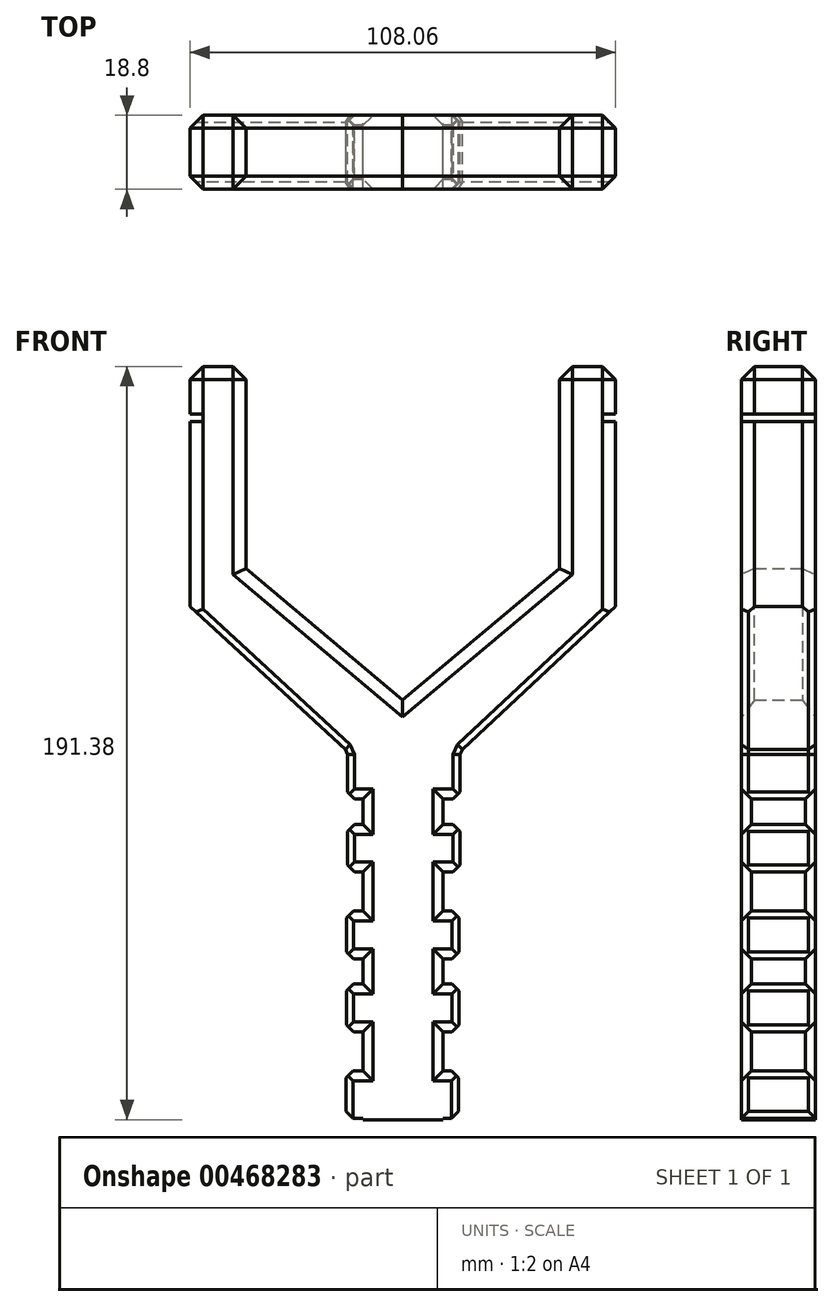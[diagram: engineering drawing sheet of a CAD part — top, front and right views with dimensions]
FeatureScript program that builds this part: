
annotation { "Feature Type Name" : "Feature", "Feature Type Description" : "" }
export const myFeature = defineFeature(function(context is Context, id is Id, definition is map)
    precondition{}
    {
        {
            var Q0;
            Q0=qCreatedBy(makeId("Front.planeOp"),FACE);
            var sketch = newSketch(context, id + "F0", { "sketchPlane" : qUnion([Q0])});
            skLineSegment(sketch, "E0.bottom", {"start": v(-10.06, -21.6) * mm, "end": v(10.26, -21.6) * mm});
            skLineSegment(sketch, "E0.top", {"start": v(-10.06, -123.2) * mm, "end": v(10.26, -123.2) * mm});
            skLineSegment(sketch, "E0.left", {"start": v(-10.06, -21.6) * mm, "end": v(-10.06, -123.2) * mm});
            skLineSegment(sketch, "E0.right", {"start": v(10.26, -21.6) * mm, "end": v(10.26, -123.2) * mm});
            skLineSegment(sketch, "E1.bottom", {"start": v(-14, -29.67) * mm, "end": v(14.56, -29.67) * mm});
            skLineSegment(sketch, "E1.top", {"start": v(-14, -41.76) * mm, "end": v(14.56, -41.76) * mm});
            skLineSegment(sketch, "E1.left", {"start": v(-14, -29.67) * mm, "end": v(-14, -41.76) * mm});
            skLineSegment(sketch, "E1.right", {"start": v(14.56, -29.67) * mm, "end": v(14.56, -41.76) * mm});
            skLineSegment(sketch, "E2.0.1.0", {"start": v(-14, -48.22) * mm, "end": v(14.56, -48.22) * mm});
            skLineSegment(sketch, "E2.0.1.1", {"start": v(-14, -60.3) * mm, "end": v(14.56, -60.3) * mm});
            skLineSegment(sketch, "E2.0.1.2", {"start": v(14.56, -48.22) * mm, "end": v(14.56, -60.3) * mm});
            skLineSegment(sketch, "E2.0.1.3", {"start": v(-14, -48.22) * mm, "end": v(-14, -60.3) * mm});
            skLineSegment(sketch, "E2.1.0.0", {"start": v(-14.22, -70.2) * mm, "end": v(14.34, -70.2) * mm});
            skLineSegment(sketch, "E2.1.0.1", {"start": v(-14.22, -82.3) * mm, "end": v(14.34, -82.3) * mm});
            skLineSegment(sketch, "E2.1.0.2", {"start": v(14.34, -70.2) * mm, "end": v(14.34, -82.3) * mm});
            skLineSegment(sketch, "E2.1.0.3", {"start": v(-14.22, -70.2) * mm, "end": v(-14.22, -82.3) * mm});
            skLineSegment(sketch, "E2.1.1.0", {"start": v(-14.22, -88.75) * mm, "end": v(14.34, -88.75) * mm});
            skLineSegment(sketch, "E2.1.1.1", {"start": v(-14.22, -100.84) * mm, "end": v(14.34, -100.84) * mm});
            skLineSegment(sketch, "E2.1.1.2", {"start": v(14.34, -88.75) * mm, "end": v(14.34, -100.84) * mm});
            skLineSegment(sketch, "E2.1.1.3", {"start": v(-14.22, -88.75) * mm, "end": v(-14.22, -100.84) * mm});
            skLineSegment(sketch, "E2.2.0.0", {"start": v(-14.44, -110.74) * mm, "end": v(14.13, -110.74) * mm});
            skLineSegment(sketch, "E2.2.0.1", {"start": v(-14.44, -122.83) * mm, "end": v(14.13, -122.83) * mm});
            skLineSegment(sketch, "E2.2.0.2", {"start": v(14.13, -110.74) * mm, "end": v(14.13, -122.83) * mm});
            skLineSegment(sketch, "E2.2.0.3", {"start": v(-14.44, -110.74) * mm, "end": v(-14.44, -122.83) * mm});
            skLineSegment(sketch, "E2.direction1", {"start": v(-14, -41.76) * mm, "end": v(-14.22, -82.3) * mm, "construction": true});
            skLineSegment(sketch, "E2.direction2", {"start": v(-14, -41.76) * mm, "end": v(-14, -60.3) * mm, "construction": true});
            skLineSegment(sketch, "E3.bottom", {"start": v(-54.03, 7.22) * mm, "end": v(-43.42, 19.87) * mm});
            skLineSegment(sketch, "E3.top", {"start": v(-10.06, -29.67) * mm, "end": v(0.55, -17.03) * mm});
            skLineSegment(sketch, "E3.left", {"start": v(-54.03, 7.22) * mm, "end": v(-10.06, -29.67) * mm});
            skLineSegment(sketch, "E3.right", {"start": v(-43.42, 19.87) * mm, "end": v(0.55, -17.03) * mm});
            skLineSegment(sketch, "E4.MirrorCS", {"start": v(43.42, 19.87) * mm, "end": v(-0.55, -17.03) * mm});
            skLineSegment(sketch, "E5.MirrorCS", {"start": v(54.03, 7.22) * mm, "end": v(43.42, 19.87) * mm});
            skLineSegment(sketch, "E6.MirrorCS", {"start": v(54.03, 7.22) * mm, "end": v(10.06, -29.67) * mm});
            skLineSegment(sketch, "E7.MirrorCS", {"start": v(10.06, -29.67) * mm, "end": v(-0.55, -17.03) * mm});
            skLineSegment(sketch, "E8.bottom", {"start": v(-54.03, 68.18) * mm, "end": v(-39.8, 68.18) * mm});
            skLineSegment(sketch, "E8.top", {"start": v(-54.03, 7.22) * mm, "end": v(-39.8, 7.22) * mm});
            skLineSegment(sketch, "E8.left", {"start": v(-54.03, 68.18) * mm, "end": v(-54.03, 7.22) * mm});
            skLineSegment(sketch, "E8.right", {"start": v(-39.8, 68.18) * mm, "end": v(-39.8, 7.22) * mm});
            skLineSegment(sketch, "E9.bottom", {"start": v(39.8, 68.18) * mm, "end": v(54.03, 68.18) * mm});
            skLineSegment(sketch, "E9.top", {"start": v(39.8, 7.22) * mm, "end": v(54.03, 7.22) * mm});
            skLineSegment(sketch, "E9.left", {"start": v(39.8, 68.18) * mm, "end": v(39.8, 7.22) * mm});
            skLineSegment(sketch, "E9.right", {"start": v(54.03, 68.18) * mm, "end": v(54.03, 7.22) * mm});
            skFitSpline(sketch, "E10", {"points": [v(-54.03, 7.22) * mm, v(-14, -29.67) * mm], "startDerivative": vector(40.02, -36.9) * mm, "endDerivative": vector(40.02, -36.9) * mm});
            skFitSpline(sketch, "E11", {"points": [v(14.56, -29.67) * mm, v(54.03, 7.22) * mm], "startDerivative": vector(39.47, 36.9) * mm, "endDerivative": vector(39.47, 36.9) * mm});
            skLineSegment(sketch, "E12.bottom", {"start": v(-54.03, 56.1) * mm, "end": v(-50.76, 56.1) * mm});
            skLineSegment(sketch, "E12.top", {"start": v(-54.03, 54.23) * mm, "end": v(-50.76, 54.23) * mm});
            skLineSegment(sketch, "E12.left", {"start": v(-54.03, 56.1) * mm, "end": v(-54.03, 54.23) * mm});
            skLineSegment(sketch, "E12.right", {"start": v(-50.76, 56.1) * mm, "end": v(-50.76, 54.23) * mm});
            skLineSegment(sketch, "E13.MirrorCS", {"start": v(54.03, 56.1) * mm, "end": v(50.76, 56.1) * mm});
            skLineSegment(sketch, "E14.MirrorCS", {"start": v(54.03, 54.23) * mm, "end": v(50.76, 54.23) * mm});
            skLineSegment(sketch, "E15.MirrorCS", {"start": v(50.76, 56.1) * mm, "end": v(50.76, 54.23) * mm});
            skLineSegment(sketch, "E16.MirrorCS", {"start": v(54.03, 56.1) * mm, "end": v(54.03, 54.23) * mm});
            skSolve(sketch);
        }
        {
            var Q0;
            {var subQ0=sQuery(id+"F0.wireOp",EDGE,"E3.top");var subQ1=sQuery(id+"F0.wireOp",EDGE,"E0.bottom");var subQ2=makeQuery(id+"F0.imprint","INTERSECT",VERTEX,{"derivedFrom":[subQ1,subQ0]});Q0=makeQuery(id+"F0.imprint","IMPRINT",FACE,{"disambiguationData":[TD([[makeQuery(id+"F0.imprint","IMPRINT",EDGE,{"disambiguationData":[TD([[subQ2,-1.0]])],"derivedFrom":subQ1}),-1.0]])]});}
            var Q1;
            {var subQ0=sQuery(id+"F0.wireOp",EDGE,"E3.top");var subQ1=sQuery(id+"F0.wireOp",EDGE,"E0.bottom");var subQ2=makeQuery(id+"F0.imprint","INTERSECT",VERTEX,{"derivedFrom":[subQ1,subQ0]});Q1=makeQuery(id+"F0.imprint","IMPRINT",FACE,{"disambiguationData":[TD([[makeQuery(id+"F0.imprint","IMPRINT",EDGE,{"disambiguationData":[TD([[subQ2,-1.0]])],"derivedFrom":subQ1}),1.0]])]});}
            var Q2;
            {var subQ0=sQuery(id+"F0.wireOp",EDGE,"E2.1.0.1");var subQ1=sQuery(id+"F0.wireOp",EDGE,"E0.left");var subQ2=makeQuery(id+"F0.imprint","INTERSECT",VERTEX,{"derivedFrom":[subQ1,subQ0]});Q2=makeQuery(id+"F0.imprint","IMPRINT",FACE,{"disambiguationData":[TD([[makeQuery(id+"F0.imprint","IMPRINT",EDGE,{"disambiguationData":[TD([[subQ2,-1.0]])],"derivedFrom":subQ1}),1.0]])]});}
            var Q3;
            {var subQ0=sQuery(id+"F0.wireOp",EDGE,"E3.bottom");Q3=makeQuery(id+"F0.imprint","IMPRINT",FACE,{"disambiguationData":[TD([[makeQuery(id+"F0.imprint","IMPRINT",EDGE,{"derivedFrom":subQ0}),-1.0]])]});}
            var Q4;
            {var subQ0=sQuery(id+"F0.wireOp",EDGE,"E2.1.1.0");var subQ1=sQuery(id+"F0.wireOp",EDGE,"E0.left");var subQ2=makeQuery(id+"F0.imprint","INTERSECT",VERTEX,{"derivedFrom":[subQ1,subQ0]});Q4=makeQuery(id+"F0.imprint","IMPRINT",FACE,{"disambiguationData":[TD([[makeQuery(id+"F0.imprint","IMPRINT",EDGE,{"disambiguationData":[TD([[subQ2,-1.0]])],"derivedFrom":subQ1}),1.0]])]});}
            var Q5;
            {var subQ0=sQuery(id+"F0.wireOp",EDGE,"E1.top");var subQ1=sQuery(id+"F0.wireOp",EDGE,"E0.left");var subQ2=makeQuery(id+"F0.imprint","INTERSECT",VERTEX,{"derivedFrom":[subQ1,subQ0]});Q5=makeQuery(id+"F0.imprint","IMPRINT",FACE,{"disambiguationData":[TD([[makeQuery(id+"F0.imprint","IMPRINT",EDGE,{"disambiguationData":[TD([[subQ2,-1.0]])],"derivedFrom":subQ1}),1.0]])]});}
            var Q6;
            {var subQ0=sQuery(id+"F0.wireOp",EDGE,"E2.1.1.1");var subQ1=sQuery(id+"F0.wireOp",EDGE,"E0.left");var subQ2=makeQuery(id+"F0.imprint","INTERSECT",VERTEX,{"derivedFrom":[subQ1,subQ0]});Q6=makeQuery(id+"F0.imprint","IMPRINT",FACE,{"disambiguationData":[TD([[makeQuery(id+"F0.imprint","IMPRINT",EDGE,{"disambiguationData":[TD([[subQ2,-1.0]])],"derivedFrom":subQ1}),1.0]])]});}
            var Q7;
            {var subQ0=sQuery(id+"F0.wireOp",EDGE,"E2.0.1.1");var subQ1=sQuery(id+"F0.wireOp",EDGE,"E0.left");var subQ2=makeQuery(id+"F0.imprint","INTERSECT",VERTEX,{"derivedFrom":[subQ1,subQ0]});Q7=makeQuery(id+"F0.imprint","IMPRINT",FACE,{"disambiguationData":[TD([[makeQuery(id+"F0.imprint","IMPRINT",EDGE,{"disambiguationData":[TD([[subQ2,-1.0]])],"derivedFrom":subQ1}),1.0]])]});}
            var Q8;
            {var subQ6=sQuery(id+"F0.wireOp",EDGE,"E9.top");Q8=makeQuery(id+"F0.imprint","IMPRINT",FACE,{"disambiguationData":[TD([[makeQuery(id+"F0.imprint","IMPRINT",EDGE,{"derivedFrom":subQ6}),-1.0]])]});}
            var Q9;
            {var subQ5=sQuery(id+"F0.wireOp",EDGE,"E2.0.1.3");Q9=makeQuery(id+"F0.imprint","IMPRINT",FACE,{"disambiguationData":[TD([[makeQuery(id+"F0.imprint","IMPRINT",EDGE,{"derivedFrom":subQ5}),1.0]])]});}
            var Q10;
            {var subQ5=sQuery(id+"F0.wireOp",EDGE,"E2.1.0.3");Q10=makeQuery(id+"F0.imprint","IMPRINT",FACE,{"disambiguationData":[TD([[makeQuery(id+"F0.imprint","IMPRINT",EDGE,{"derivedFrom":subQ5}),1.0]])]});}
            var Q11;
            {var subQ5=sQuery(id+"F0.wireOp",EDGE,"E2.1.1.3");Q11=makeQuery(id+"F0.imprint","IMPRINT",FACE,{"disambiguationData":[TD([[makeQuery(id+"F0.imprint","IMPRINT",EDGE,{"derivedFrom":subQ5}),1.0]])]});}
            var Q12;
            {var subQ5=sQuery(id+"F0.wireOp",EDGE,"E2.2.0.3");Q12=makeQuery(id+"F0.imprint","IMPRINT",FACE,{"disambiguationData":[TD([[makeQuery(id+"F0.imprint","IMPRINT",EDGE,{"derivedFrom":subQ5}),1.0]])]});}
            var Q13;
            {var subQ5=sQuery(id+"F0.wireOp",EDGE,"E2.0.1.2");Q13=makeQuery(id+"F0.imprint","IMPRINT",FACE,{"disambiguationData":[TD([[makeQuery(id+"F0.imprint","IMPRINT",EDGE,{"derivedFrom":subQ5}),-1.0]])]});}
            var Q14;
            {var subQ5=sQuery(id+"F0.wireOp",EDGE,"E2.2.0.2");Q14=makeQuery(id+"F0.imprint","IMPRINT",FACE,{"disambiguationData":[TD([[makeQuery(id+"F0.imprint","IMPRINT",EDGE,{"derivedFrom":subQ5}),-1.0]])]});}
            var Q15;
            {var subQ5=sQuery(id+"F0.wireOp",EDGE,"E2.1.0.2");Q15=makeQuery(id+"F0.imprint","IMPRINT",FACE,{"disambiguationData":[TD([[makeQuery(id+"F0.imprint","IMPRINT",EDGE,{"derivedFrom":subQ5}),-1.0]])]});}
            var Q16;
            {var subQ5=sQuery(id+"F0.wireOp",EDGE,"E2.1.1.2");Q16=makeQuery(id+"F0.imprint","IMPRINT",FACE,{"disambiguationData":[TD([[makeQuery(id+"F0.imprint","IMPRINT",EDGE,{"derivedFrom":subQ5}),-1.0]])]});}
            var Q17;
            {var subQ2=sQuery(id+"F0.wireOp",EDGE,"E3.bottom");Q17=makeQuery(id+"F0.imprint","IMPRINT",FACE,{"disambiguationData":[TD([[makeQuery(id+"F0.imprint","IMPRINT",EDGE,{"derivedFrom":subQ2}),1.0]])]});}
            var Q18;
            {var subQ4=sQuery(id+"F0.wireOp",EDGE,"E5.MirrorCS");Q18=makeQuery(id+"F0.imprint","IMPRINT",FACE,{"disambiguationData":[TD([[makeQuery(id+"F0.imprint","IMPRINT",EDGE,{"derivedFrom":subQ4}),-1.0]])]});}
            var Q19;
            {var subQ0=sQuery(id+"F0.wireOp",EDGE,"E0.left");var subQ1=sQuery(id+"F0.wireOp",EDGE,"E0.bottom");var subQ2=makeQuery(id+"F0.imprint","INTERSECT",VERTEX,{"derivedFrom":[subQ1,subQ0]});Q19=makeQuery(id+"F0.imprint","IMPRINT",FACE,{"disambiguationData":[TD([[makeQuery(id+"F0.imprint","IMPRINT",EDGE,{"disambiguationData":[TD([[subQ2,-1.0]])],"derivedFrom":subQ1}),-1.0]])]});}
            var Q20;
            {var subQ5=sQuery(id+"F0.wireOp",EDGE,"E1.left");Q20=makeQuery(id+"F0.imprint","IMPRINT",FACE,{"disambiguationData":[TD([[makeQuery(id+"F0.imprint","IMPRINT",EDGE,{"derivedFrom":subQ5}),1.0]])]});}
            var Q21;
            {var subQ0=sQuery(id+"F0.wireOp",EDGE,"E2.0.1.0");var subQ1=sQuery(id+"F0.wireOp",EDGE,"E0.left");var subQ2=makeQuery(id+"F0.imprint","INTERSECT",VERTEX,{"derivedFrom":[subQ1,subQ0]});Q21=makeQuery(id+"F0.imprint","IMPRINT",FACE,{"disambiguationData":[TD([[makeQuery(id+"F0.imprint","IMPRINT",EDGE,{"disambiguationData":[TD([[subQ2,-1.0]])],"derivedFrom":subQ1}),1.0]])]});}
            var Q22;
            {var subQ0=sQuery(id+"F0.wireOp",EDGE,"E0.right");var subQ1=sQuery(id+"F0.wireOp",EDGE,"E0.bottom");var subQ2=makeQuery(id+"F0.imprint","INTERSECT",VERTEX,{"derivedFrom":[subQ1,subQ0]});Q22=makeQuery(id+"F0.imprint","IMPRINT",FACE,{"disambiguationData":[TD([[makeQuery(id+"F0.imprint","IMPRINT",EDGE,{"disambiguationData":[TD([[subQ2,1.0]])],"derivedFrom":subQ1}),-1.0]])]});}
            var Q23;
            {var subQ0=sQuery(id+"F0.wireOp",EDGE,"E5.MirrorCS");Q23=makeQuery(id+"F0.imprint","IMPRINT",FACE,{"disambiguationData":[TD([[makeQuery(id+"F0.imprint","IMPRINT",EDGE,{"derivedFrom":subQ0}),1.0]])]});}
            var Q24;
            {var subQ0=sQuery(id+"F0.wireOp",EDGE,"E2.2.0.0");var subQ1=sQuery(id+"F0.wireOp",EDGE,"E0.left");var subQ2=makeQuery(id+"F0.imprint","INTERSECT",VERTEX,{"derivedFrom":[subQ1,subQ0]});Q24=makeQuery(id+"F0.imprint","IMPRINT",FACE,{"disambiguationData":[TD([[makeQuery(id+"F0.imprint","IMPRINT",EDGE,{"disambiguationData":[TD([[subQ2,-1.0]])],"derivedFrom":subQ1}),1.0]])]});}
            var Q25;
            {var subQ5=sQuery(id+"F0.wireOp",EDGE,"E1.right");Q25=makeQuery(id+"F0.imprint","IMPRINT",FACE,{"disambiguationData":[TD([[makeQuery(id+"F0.imprint","IMPRINT",EDGE,{"derivedFrom":subQ5}),-1.0]])]});}
            var Q26;
            {var subQ2=sQuery(id+"F0.wireOp",EDGE,"E0.right");var subQ6=sQuery(id+"F0.wireOp",EDGE,"E1.top");var subQ7=makeQuery(id+"F0.imprint","INTERSECT",VERTEX,{"derivedFrom":[subQ2,subQ6]});Q26=makeQuery(id+"F0.imprint","IMPRINT",FACE,{"disambiguationData":[TD([[makeQuery(id+"F0.imprint","IMPRINT",EDGE,{"disambiguationData":[TD([[subQ7,1.0]])],"derivedFrom":subQ2}),-1.0]])]});}
            var Q27;
            {var subQ0=sQuery(id+"F0.wireOp",EDGE,"E2.1.0.0");var subQ1=sQuery(id+"F0.wireOp",EDGE,"E0.left");var subQ2=makeQuery(id+"F0.imprint","INTERSECT",VERTEX,{"derivedFrom":[subQ1,subQ0]});Q27=makeQuery(id+"F0.imprint","IMPRINT",FACE,{"disambiguationData":[TD([[makeQuery(id+"F0.imprint","IMPRINT",EDGE,{"disambiguationData":[TD([[subQ2,-1.0]])],"derivedFrom":subQ1}),1.0]])]});}
            var Q28;
            {var subQ2=sQuery(id+"F0.wireOp",EDGE,"E3.left");Q28=makeQuery(id+"F0.imprint","IMPRINT",FACE,{"disambiguationData":[TD([[makeQuery(id+"F0.imprint","IMPRINT",EDGE,{"derivedFrom":subQ2}),-1.0]])]});}
            var Q29;
            {var subQ0=sQuery(id+"F0.wireOp",EDGE,"E3.left");Q29=makeQuery(id+"F0.imprint","IMPRINT",FACE,{"disambiguationData":[TD([[makeQuery(id+"F0.imprint","IMPRINT",EDGE,{"derivedFrom":subQ0}),1.0]])]});}
            var Q30;
            {var subQ5=sQuery(id+"F0.wireOp",EDGE,"E11");Q30=makeQuery(id+"F0.imprint","IMPRINT",FACE,{"disambiguationData":[TD([[makeQuery(id+"F0.imprint","IMPRINT",EDGE,{"derivedFrom":subQ5}),1.0]])]});}
            var Q31;
            {var subQ0=sQuery(id+"F0.wireOp",EDGE,"E0.top");Q31=makeQuery(id+"F0.imprint","IMPRINT",FACE,{"disambiguationData":[TD([[makeQuery(id+"F0.imprint","IMPRINT",EDGE,{"derivedFrom":subQ0}),1.0]])]});}
            var Q32;
            {var subQ0=sQuery(id+"F0.wireOp",EDGE,"E3.right");var subQ1=sQuery(id+"F0.wireOp",EDGE,"E3.top");var subQ2=makeQuery(id+"F0.imprint","INTERSECT",VERTEX,{"derivedFrom":[subQ1,subQ0]});Q32=makeQuery(id+"F0.imprint","IMPRINT",FACE,{"disambiguationData":[TD([[makeQuery(id+"F0.imprint","IMPRINT",EDGE,{"disambiguationData":[TD([[subQ2,1.0]])],"derivedFrom":subQ1}),1.0]])]});}
            var Q33;
            {var subQ0=sQuery(id+"F0.wireOp",EDGE,"E6.MirrorCS");var subQ1=sQuery(id+"F0.wireOp",EDGE,"E0.right");var subQ2=makeQuery(id+"F0.imprint","INTERSECT",VERTEX,{"derivedFrom":[subQ1,subQ0]});Q33=makeQuery(id+"F0.imprint","IMPRINT",FACE,{"disambiguationData":[TD([[makeQuery(id+"F0.imprint","IMPRINT",EDGE,{"disambiguationData":[TD([[subQ2,-1.0]])],"derivedFrom":subQ1}),-1.0]])]});}
            extrude(context, id + "F1", {"entities" : qUnion([Q0, Q1, Q2, Q3, Q4, Q5, Q6, Q7, Q8, Q9, Q10, Q11, Q12, Q13, Q14, Q15, Q16, Q17, Q18, Q19, Q20, Q21, Q22, Q23, Q24, Q25, Q26, Q27, Q28, Q29, Q30, Q31, Q32, Q33]), "depth" : 18.8 * mm});
        }
        {
            var Q0;
            Q0=makeQuery(id+"F1.opExtrude","SWEPT_EDGE",EDGE,{"disambiguationData":[OSD([sQuery(id+"F0.wireOp",EDGE,"E1.top"),sQuery(id+"F0.wireOp",EDGE,"E1.left")])]});
            var Q1;
            Q1=makeQuery(id+"F1.opExtrude","CAP_EDGE",EDGE,{"disambiguationData":[OSD([sQuery(id+"F0.wireOp",EDGE,"E1.left")])],"isStart":true});
            var Q2;
            Q2=makeQuery(id+"F1.opExtrude","SWEPT_EDGE",EDGE,{"disambiguationData":[OSD([sQuery(id+"F0.wireOp",EDGE,"E1.bottom"),sQuery(id+"F0.wireOp",EDGE,"E1.left"),sQuery(id+"F0.wireOp",EDGE,"E10")])]});
            var Q3;
            Q3=makeQuery(id+"F1.opExtrude","CAP_EDGE",EDGE,{"disambiguationData":[OSD([sQuery(id+"F0.wireOp",EDGE,"E1.left")])],"isStart":false});
            var Q4;
            Q4=makeQuery(id+"F1.opExtrude","SWEPT_EDGE",EDGE,{"disambiguationData":[OSD([sQuery(id+"F0.wireOp",EDGE,"E2.0.1.0"),sQuery(id+"F0.wireOp",EDGE,"E2.0.1.3")])]});
            var Q5;
            Q5=makeQuery(id+"F1.opExtrude","CAP_EDGE",EDGE,{"disambiguationData":[OSD([sQuery(id+"F0.wireOp",EDGE,"E2.0.1.3")])],"isStart":true});
            var Q6;
            Q6=makeQuery(id+"F1.opExtrude","SWEPT_EDGE",EDGE,{"disambiguationData":[OSD([sQuery(id+"F0.wireOp",EDGE,"E2.0.1.1"),sQuery(id+"F0.wireOp",EDGE,"E2.0.1.3")])]});
            var Q7;
            Q7=makeQuery(id+"F1.opExtrude","CAP_EDGE",EDGE,{"disambiguationData":[OSD([sQuery(id+"F0.wireOp",EDGE,"E2.0.1.3")])],"isStart":false});
            var Q8;
            Q8=makeQuery(id+"F1.opExtrude","SWEPT_EDGE",EDGE,{"disambiguationData":[OSD([sQuery(id+"F0.wireOp",EDGE,"E2.1.0.0"),sQuery(id+"F0.wireOp",EDGE,"E2.1.0.3")])]});
            var Q9;
            Q9=makeQuery(id+"F1.opExtrude","SWEPT_EDGE",EDGE,{"disambiguationData":[OSD([sQuery(id+"F0.wireOp",EDGE,"E2.1.0.1"),sQuery(id+"F0.wireOp",EDGE,"E2.1.0.3")])]});
            var Q10;
            Q10=makeQuery(id+"F1.opExtrude","CAP_EDGE",EDGE,{"disambiguationData":[OSD([sQuery(id+"F0.wireOp",EDGE,"E2.1.0.3")])],"isStart":true});
            var Q11;
            Q11=makeQuery(id+"F1.opExtrude","CAP_EDGE",EDGE,{"disambiguationData":[OSD([sQuery(id+"F0.wireOp",EDGE,"E2.1.0.3")])],"isStart":false});
            var Q12;
            Q12=makeQuery(id+"F1.opExtrude","SWEPT_EDGE",EDGE,{"disambiguationData":[OSD([sQuery(id+"F0.wireOp",EDGE,"E2.1.1.0"),sQuery(id+"F0.wireOp",EDGE,"E2.1.1.3")])]});
            var Q13;
            Q13=makeQuery(id+"F1.opExtrude","SWEPT_EDGE",EDGE,{"disambiguationData":[OSD([sQuery(id+"F0.wireOp",EDGE,"E2.1.1.1"),sQuery(id+"F0.wireOp",EDGE,"E2.1.1.3")])]});
            var Q14;
            Q14=makeQuery(id+"F1.opExtrude","CAP_EDGE",EDGE,{"disambiguationData":[OSD([sQuery(id+"F0.wireOp",EDGE,"E2.1.1.3")])],"isStart":false});
            var Q15;
            Q15=makeQuery(id+"F1.opExtrude","CAP_EDGE",EDGE,{"disambiguationData":[OSD([sQuery(id+"F0.wireOp",EDGE,"E2.1.1.3")])],"isStart":true});
            var Q16;
            Q16=makeQuery(id+"F1.opExtrude","SWEPT_EDGE",EDGE,{"disambiguationData":[OSD([sQuery(id+"F0.wireOp",EDGE,"E2.2.0.0"),sQuery(id+"F0.wireOp",EDGE,"E2.2.0.3")])]});
            var Q17;
            Q17=makeQuery(id+"F1.opExtrude","CAP_EDGE",EDGE,{"disambiguationData":[OSD([sQuery(id+"F0.wireOp",EDGE,"E2.2.0.3")])],"isStart":true});
            var Q18;
            Q18=makeQuery(id+"F1.opExtrude","CAP_EDGE",EDGE,{"disambiguationData":[OSD([sQuery(id+"F0.wireOp",EDGE,"E2.2.0.3")])],"isStart":false});
            var Q19;
            Q19=makeQuery(id+"F1.opExtrude","SWEPT_EDGE",EDGE,{"disambiguationData":[OSD([sQuery(id+"F0.wireOp",EDGE,"E2.2.0.1"),sQuery(id+"F0.wireOp",EDGE,"E2.2.0.3")])]});
            var Q20;
            Q20=makeQuery(id+"F1.opExtrude","SWEPT_EDGE",EDGE,{"disambiguationData":[OSD([sQuery(id+"F0.wireOp",EDGE,"E2.2.0.0"),sQuery(id+"F0.wireOp",EDGE,"E2.2.0.2")])]});
            var Q21;
            Q21=makeQuery(id+"F1.opExtrude","CAP_EDGE",EDGE,{"disambiguationData":[OSD([sQuery(id+"F0.wireOp",EDGE,"E2.2.0.2")])],"isStart":false});
            var Q22;
            Q22=makeQuery(id+"F1.opExtrude","SWEPT_EDGE",EDGE,{"disambiguationData":[OSD([sQuery(id+"F0.wireOp",EDGE,"E2.2.0.1"),sQuery(id+"F0.wireOp",EDGE,"E2.2.0.2")])]});
            var Q23;
            Q23=makeQuery(id+"F1.opExtrude","CAP_EDGE",EDGE,{"disambiguationData":[OSD([sQuery(id+"F0.wireOp",EDGE,"E2.2.0.2")])],"isStart":true});
            var Q24;
            Q24=makeQuery(id+"F1.opExtrude","SWEPT_EDGE",EDGE,{"disambiguationData":[OSD([sQuery(id+"F0.wireOp",EDGE,"E2.1.1.1"),sQuery(id+"F0.wireOp",EDGE,"E2.1.1.2")])]});
            var Q25;
            Q25=makeQuery(id+"F1.opExtrude","SWEPT_EDGE",EDGE,{"disambiguationData":[OSD([sQuery(id+"F0.wireOp",EDGE,"E2.1.1.0"),sQuery(id+"F0.wireOp",EDGE,"E2.1.1.2")])]});
            var Q26;
            Q26=makeQuery(id+"F1.opExtrude","CAP_EDGE",EDGE,{"disambiguationData":[OSD([sQuery(id+"F0.wireOp",EDGE,"E2.1.1.2")])],"isStart":true});
            var Q27;
            Q27=makeQuery(id+"F1.opExtrude","CAP_EDGE",EDGE,{"disambiguationData":[OSD([sQuery(id+"F0.wireOp",EDGE,"E2.1.1.2")])],"isStart":false});
            var Q28;
            Q28=makeQuery(id+"F1.opExtrude","SWEPT_EDGE",EDGE,{"disambiguationData":[OSD([sQuery(id+"F0.wireOp",EDGE,"E2.1.0.1"),sQuery(id+"F0.wireOp",EDGE,"E2.1.0.2")])]});
            var Q29;
            Q29=makeQuery(id+"F1.opExtrude","CAP_EDGE",EDGE,{"disambiguationData":[OSD([sQuery(id+"F0.wireOp",EDGE,"E2.1.0.2")])],"isStart":false});
            var Q30;
            Q30=makeQuery(id+"F1.opExtrude","SWEPT_EDGE",EDGE,{"disambiguationData":[OSD([sQuery(id+"F0.wireOp",EDGE,"E2.1.0.0"),sQuery(id+"F0.wireOp",EDGE,"E2.1.0.2")])]});
            var Q31;
            Q31=makeQuery(id+"F1.opExtrude","CAP_EDGE",EDGE,{"disambiguationData":[OSD([sQuery(id+"F0.wireOp",EDGE,"E2.1.0.2")])],"isStart":true});
            var Q32;
            Q32=makeQuery(id+"F1.opExtrude","SWEPT_EDGE",EDGE,{"disambiguationData":[OSD([sQuery(id+"F0.wireOp",EDGE,"E2.0.1.1"),sQuery(id+"F0.wireOp",EDGE,"E2.0.1.2")])]});
            var Q33;
            Q33=makeQuery(id+"F1.opExtrude","CAP_EDGE",EDGE,{"disambiguationData":[OSD([sQuery(id+"F0.wireOp",EDGE,"E2.0.1.2")])],"isStart":false});
            var Q34;
            Q34=makeQuery(id+"F1.opExtrude","SWEPT_EDGE",EDGE,{"disambiguationData":[OSD([sQuery(id+"F0.wireOp",EDGE,"E2.0.1.0"),sQuery(id+"F0.wireOp",EDGE,"E2.0.1.2")])]});
            var Q35;
            Q35=makeQuery(id+"F1.opExtrude","CAP_EDGE",EDGE,{"disambiguationData":[OSD([sQuery(id+"F0.wireOp",EDGE,"E2.0.1.2")])],"isStart":true});
            var Q36;
            Q36=makeQuery(id+"F1.opExtrude","SWEPT_EDGE",EDGE,{"disambiguationData":[OSD([sQuery(id+"F0.wireOp",EDGE,"E1.top"),sQuery(id+"F0.wireOp",EDGE,"E1.right")])]});
            var Q37;
            Q37=makeQuery(id+"F1.opExtrude","CAP_EDGE",EDGE,{"disambiguationData":[OSD([sQuery(id+"F0.wireOp",EDGE,"E1.right")])],"isStart":false});
            var Q38;
            Q38=makeQuery(id+"F1.opExtrude","SWEPT_EDGE",EDGE,{"disambiguationData":[OSD([sQuery(id+"F0.wireOp",EDGE,"E1.bottom"),sQuery(id+"F0.wireOp",EDGE,"E1.right"),sQuery(id+"F0.wireOp",EDGE,"E11")])]});
            var Q39;
            Q39=makeQuery(id+"F1.opExtrude","CAP_EDGE",EDGE,{"disambiguationData":[OSD([sQuery(id+"F0.wireOp",EDGE,"E1.right")])],"isStart":true});
            chamfer(context, id + "F2", {"entities" : qUnion([Q0, Q1, Q2, Q3, Q4, Q5, Q6, Q7, Q8, Q9, Q10, Q11, Q12, Q13, Q14, Q15, Q16, Q17, Q18, Q19, Q20, Q21, Q22, Q23, Q24, Q25, Q26, Q27, Q28, Q29, Q30, Q31, Q32, Q33, Q34, Q35, Q36, Q37, Q38, Q39]), "width" : 1.78 * mm, "tangentPropagation" : true});
        }
        {
            var Q0;
            {var subQ0=sQuery(id+"F0.wireOp",EDGE,"E0.left");Q0=makeQuery(id+"F1.opExtrude","CAP_EDGE",EDGE,{"disambiguationData":[OSD([subQ0]),TDD([makeQuery(id+"F0.imprint","IMPRINT",EDGE,{"disambiguationData":[TD([[makeQuery(id+"F0.imprint","INTERSECT",VERTEX,{"derivedFrom":[subQ0,sQuery(id+"F0.wireOp",EDGE,"E1.top")]}),-1.0]])],"derivedFrom":subQ0})])],"isStart":false});}
            var Q1;
            {var subQ0=sQuery(id+"F0.wireOp",EDGE,"E1.top");Q1=makeQuery(id+"F1.opExtrude","CAP_EDGE",EDGE,{"disambiguationData":[OSD([subQ0]),TDD([makeQuery(id+"F0.imprint","IMPRINT",EDGE,{"disambiguationData":[TD([[makeQuery(id+"F0.imprint","INTERSECT",VERTEX,{"derivedFrom":[subQ0,sQuery(id+"F0.wireOp",EDGE,"E1.left")]}),-1.0]])],"derivedFrom":subQ0})])],"isStart":false});}
            var Q2;
            {var subQ0=sQuery(id+"F0.wireOp",EDGE,"E1.top");Q2=makeQuery(id+"F1.opExtrude","CAP_EDGE",EDGE,{"disambiguationData":[OSD([subQ0]),TDD([makeQuery(id+"F0.imprint","IMPRINT",EDGE,{"disambiguationData":[TD([[makeQuery(id+"F0.imprint","INTERSECT",VERTEX,{"derivedFrom":[subQ0,sQuery(id+"F0.wireOp",EDGE,"E1.left")]}),-1.0]])],"derivedFrom":subQ0})])],"isStart":true});}
            var Q3;
            {var subQ0=sQuery(id+"F0.wireOp",EDGE,"E0.left");Q3=makeQuery(id+"F1.opExtrude","CAP_EDGE",EDGE,{"disambiguationData":[OSD([subQ0]),TDD([makeQuery(id+"F0.imprint","IMPRINT",EDGE,{"disambiguationData":[TD([[makeQuery(id+"F0.imprint","INTERSECT",VERTEX,{"derivedFrom":[subQ0,sQuery(id+"F0.wireOp",EDGE,"E1.top")]}),-1.0]])],"derivedFrom":subQ0})])],"isStart":true});}
            var Q4;
            {var subQ0=sQuery(id+"F0.wireOp",EDGE,"E2.0.1.0");Q4=makeQuery(id+"F1.opExtrude","CAP_EDGE",EDGE,{"disambiguationData":[OSD([subQ0]),TDD([makeQuery(id+"F0.imprint","IMPRINT",EDGE,{"disambiguationData":[TD([[makeQuery(id+"F0.imprint","INTERSECT",VERTEX,{"derivedFrom":[subQ0,sQuery(id+"F0.wireOp",EDGE,"E2.0.1.3")]}),-1.0]])],"derivedFrom":subQ0})])],"isStart":true});}
            var Q5;
            {var subQ0=sQuery(id+"F0.wireOp",EDGE,"E2.0.1.1");Q5=makeQuery(id+"F1.opExtrude","CAP_EDGE",EDGE,{"disambiguationData":[OSD([subQ0]),TDD([makeQuery(id+"F0.imprint","IMPRINT",EDGE,{"disambiguationData":[TD([[makeQuery(id+"F0.imprint","INTERSECT",VERTEX,{"derivedFrom":[subQ0,sQuery(id+"F0.wireOp",EDGE,"E2.0.1.3")]}),-1.0]])],"derivedFrom":subQ0})])],"isStart":true});}
            var Q6;
            {var subQ0=sQuery(id+"F0.wireOp",EDGE,"E0.left");Q6=makeQuery(id+"F1.opExtrude","CAP_EDGE",EDGE,{"disambiguationData":[OSD([subQ0]),TDD([makeQuery(id+"F0.imprint","IMPRINT",EDGE,{"disambiguationData":[TD([[makeQuery(id+"F0.imprint","INTERSECT",VERTEX,{"derivedFrom":[subQ0,sQuery(id+"F0.wireOp",EDGE,"E2.0.1.1")]}),-1.0]])],"derivedFrom":subQ0})])],"isStart":true});}
            var Q7;
            {var subQ0=sQuery(id+"F0.wireOp",EDGE,"E2.1.0.0");Q7=makeQuery(id+"F1.opExtrude","CAP_EDGE",EDGE,{"disambiguationData":[OSD([subQ0]),TDD([makeQuery(id+"F0.imprint","IMPRINT",EDGE,{"disambiguationData":[TD([[makeQuery(id+"F0.imprint","INTERSECT",VERTEX,{"derivedFrom":[subQ0,sQuery(id+"F0.wireOp",EDGE,"E2.1.0.3")]}),-1.0]])],"derivedFrom":subQ0})])],"isStart":true});}
            var Q8;
            {var subQ0=sQuery(id+"F0.wireOp",EDGE,"E2.1.0.1");Q8=makeQuery(id+"F1.opExtrude","CAP_EDGE",EDGE,{"disambiguationData":[OSD([subQ0]),TDD([makeQuery(id+"F0.imprint","IMPRINT",EDGE,{"disambiguationData":[TD([[makeQuery(id+"F0.imprint","INTERSECT",VERTEX,{"derivedFrom":[subQ0,sQuery(id+"F0.wireOp",EDGE,"E2.1.0.3")]}),-1.0]])],"derivedFrom":subQ0})])],"isStart":true});}
            var Q9;
            {var subQ0=sQuery(id+"F0.wireOp",EDGE,"E0.left");Q9=makeQuery(id+"F1.opExtrude","CAP_EDGE",EDGE,{"disambiguationData":[OSD([subQ0]),TDD([makeQuery(id+"F0.imprint","IMPRINT",EDGE,{"disambiguationData":[TD([[makeQuery(id+"F0.imprint","INTERSECT",VERTEX,{"derivedFrom":[subQ0,sQuery(id+"F0.wireOp",EDGE,"E2.1.0.1")]}),-1.0]])],"derivedFrom":subQ0})])],"isStart":true});}
            var Q10;
            {var subQ0=sQuery(id+"F0.wireOp",EDGE,"E2.1.1.1");Q10=makeQuery(id+"F1.opExtrude","CAP_EDGE",EDGE,{"disambiguationData":[OSD([subQ0]),TDD([makeQuery(id+"F0.imprint","IMPRINT",EDGE,{"disambiguationData":[TD([[makeQuery(id+"F0.imprint","INTERSECT",VERTEX,{"derivedFrom":[subQ0,sQuery(id+"F0.wireOp",EDGE,"E2.1.1.3")]}),-1.0]])],"derivedFrom":subQ0})])],"isStart":true});}
            var Q11;
            {var subQ0=sQuery(id+"F0.wireOp",EDGE,"E0.left");Q11=makeQuery(id+"F1.opExtrude","CAP_EDGE",EDGE,{"disambiguationData":[OSD([subQ0]),TDD([makeQuery(id+"F0.imprint","IMPRINT",EDGE,{"disambiguationData":[TD([[makeQuery(id+"F0.imprint","INTERSECT",VERTEX,{"derivedFrom":[subQ0,sQuery(id+"F0.wireOp",EDGE,"E2.1.1.1")]}),-1.0]])],"derivedFrom":subQ0})])],"isStart":true});}
            var Q12;
            {var subQ0=sQuery(id+"F0.wireOp",EDGE,"E2.2.0.0");Q12=makeQuery(id+"F1.opExtrude","CAP_EDGE",EDGE,{"disambiguationData":[OSD([subQ0]),TDD([makeQuery(id+"F0.imprint","IMPRINT",EDGE,{"disambiguationData":[TD([[makeQuery(id+"F0.imprint","INTERSECT",VERTEX,{"derivedFrom":[subQ0,sQuery(id+"F0.wireOp",EDGE,"E2.2.0.3")]}),-1.0]])],"derivedFrom":subQ0})])],"isStart":true});}
            var Q13;
            {var subQ0=sQuery(id+"F0.wireOp",EDGE,"E2.2.0.0");Q13=makeQuery(id+"F1.opExtrude","CAP_EDGE",EDGE,{"disambiguationData":[OSD([subQ0]),TDD([makeQuery(id+"F0.imprint","IMPRINT",EDGE,{"disambiguationData":[TD([[makeQuery(id+"F0.imprint","INTERSECT",VERTEX,{"derivedFrom":[subQ0,sQuery(id+"F0.wireOp",EDGE,"E2.2.0.2")]}),1.0]])],"derivedFrom":subQ0})])],"isStart":true});}
            var Q14;
            {var subQ0=sQuery(id+"F0.wireOp",EDGE,"E0.right");Q14=makeQuery(id+"F1.opExtrude","CAP_EDGE",EDGE,{"disambiguationData":[OSD([subQ0]),TDD([makeQuery(id+"F0.imprint","IMPRINT",EDGE,{"disambiguationData":[TD([[makeQuery(id+"F0.imprint","INTERSECT",VERTEX,{"derivedFrom":[subQ0,sQuery(id+"F0.wireOp",EDGE,"E2.1.1.1")]}),-1.0]])],"derivedFrom":subQ0})])],"isStart":true});}
            var Q15;
            {var subQ0=sQuery(id+"F0.wireOp",EDGE,"E2.1.1.1");Q15=makeQuery(id+"F1.opExtrude","CAP_EDGE",EDGE,{"disambiguationData":[OSD([subQ0]),TDD([makeQuery(id+"F0.imprint","IMPRINT",EDGE,{"disambiguationData":[TD([[makeQuery(id+"F0.imprint","INTERSECT",VERTEX,{"derivedFrom":[subQ0,sQuery(id+"F0.wireOp",EDGE,"E2.1.1.2")]}),1.0]])],"derivedFrom":subQ0})])],"isStart":true});}
            var Q16;
            {var subQ0=sQuery(id+"F0.wireOp",EDGE,"E0.right");Q16=makeQuery(id+"F1.opExtrude","CAP_EDGE",EDGE,{"disambiguationData":[OSD([subQ0]),TDD([makeQuery(id+"F0.imprint","IMPRINT",EDGE,{"disambiguationData":[TD([[makeQuery(id+"F0.imprint","INTERSECT",VERTEX,{"derivedFrom":[subQ0,sQuery(id+"F0.wireOp",EDGE,"E2.1.0.1")]}),-1.0]])],"derivedFrom":subQ0})])],"isStart":true});}
            var Q17;
            {var subQ0=sQuery(id+"F0.wireOp",EDGE,"E2.1.1.0");Q17=makeQuery(id+"F1.opExtrude","CAP_EDGE",EDGE,{"disambiguationData":[OSD([subQ0]),TDD([makeQuery(id+"F0.imprint","IMPRINT",EDGE,{"disambiguationData":[TD([[makeQuery(id+"F0.imprint","INTERSECT",VERTEX,{"derivedFrom":[subQ0,sQuery(id+"F0.wireOp",EDGE,"E2.1.1.2")]}),1.0]])],"derivedFrom":subQ0})])],"isStart":true});}
            var Q18;
            {var subQ0=sQuery(id+"F0.wireOp",EDGE,"E2.1.0.1");Q18=makeQuery(id+"F1.opExtrude","CAP_EDGE",EDGE,{"disambiguationData":[OSD([subQ0]),TDD([makeQuery(id+"F0.imprint","IMPRINT",EDGE,{"disambiguationData":[TD([[makeQuery(id+"F0.imprint","INTERSECT",VERTEX,{"derivedFrom":[subQ0,sQuery(id+"F0.wireOp",EDGE,"E2.1.0.2")]}),1.0]])],"derivedFrom":subQ0})])],"isStart":true});}
            var Q19;
            {var subQ0=sQuery(id+"F0.wireOp",EDGE,"E2.1.0.0");Q19=makeQuery(id+"F1.opExtrude","CAP_EDGE",EDGE,{"disambiguationData":[OSD([subQ0]),TDD([makeQuery(id+"F0.imprint","IMPRINT",EDGE,{"disambiguationData":[TD([[makeQuery(id+"F0.imprint","INTERSECT",VERTEX,{"derivedFrom":[subQ0,sQuery(id+"F0.wireOp",EDGE,"E2.1.0.2")]}),1.0]])],"derivedFrom":subQ0})])],"isStart":true});}
            var Q20;
            {var subQ0=sQuery(id+"F0.wireOp",EDGE,"E0.right");Q20=makeQuery(id+"F1.opExtrude","CAP_EDGE",EDGE,{"disambiguationData":[OSD([subQ0]),TDD([makeQuery(id+"F0.imprint","IMPRINT",EDGE,{"disambiguationData":[TD([[makeQuery(id+"F0.imprint","INTERSECT",VERTEX,{"derivedFrom":[subQ0,sQuery(id+"F0.wireOp",EDGE,"E2.0.1.1")]}),-1.0]])],"derivedFrom":subQ0})])],"isStart":true});}
            var Q21;
            {var subQ0=sQuery(id+"F0.wireOp",EDGE,"E2.0.1.1");Q21=makeQuery(id+"F1.opExtrude","CAP_EDGE",EDGE,{"disambiguationData":[OSD([subQ0]),TDD([makeQuery(id+"F0.imprint","IMPRINT",EDGE,{"disambiguationData":[TD([[makeQuery(id+"F0.imprint","INTERSECT",VERTEX,{"derivedFrom":[subQ0,sQuery(id+"F0.wireOp",EDGE,"E2.0.1.2")]}),1.0]])],"derivedFrom":subQ0})])],"isStart":true});}
            var Q22;
            {var subQ0=sQuery(id+"F0.wireOp",EDGE,"E2.0.1.0");Q22=makeQuery(id+"F1.opExtrude","CAP_EDGE",EDGE,{"disambiguationData":[OSD([subQ0]),TDD([makeQuery(id+"F0.imprint","IMPRINT",EDGE,{"disambiguationData":[TD([[makeQuery(id+"F0.imprint","INTERSECT",VERTEX,{"derivedFrom":[subQ0,sQuery(id+"F0.wireOp",EDGE,"E2.0.1.2")]}),1.0]])],"derivedFrom":subQ0})])],"isStart":true});}
            var Q23;
            {var subQ0=sQuery(id+"F0.wireOp",EDGE,"E0.right");Q23=makeQuery(id+"F1.opExtrude","CAP_EDGE",EDGE,{"disambiguationData":[OSD([subQ0]),TDD([makeQuery(id+"F0.imprint","IMPRINT",EDGE,{"disambiguationData":[TD([[makeQuery(id+"F0.imprint","INTERSECT",VERTEX,{"derivedFrom":[subQ0,sQuery(id+"F0.wireOp",EDGE,"E1.top")]}),-1.0]])],"derivedFrom":subQ0})])],"isStart":true});}
            var Q24;
            {var subQ0=sQuery(id+"F0.wireOp",EDGE,"E1.top");Q24=makeQuery(id+"F1.opExtrude","CAP_EDGE",EDGE,{"disambiguationData":[OSD([subQ0]),TDD([makeQuery(id+"F0.imprint","IMPRINT",EDGE,{"disambiguationData":[TD([[makeQuery(id+"F0.imprint","INTERSECT",VERTEX,{"derivedFrom":[subQ0,sQuery(id+"F0.wireOp",EDGE,"E1.right")]}),1.0]])],"derivedFrom":subQ0})])],"isStart":true});}
            var Q25;
            {var subQ0=sQuery(id+"F0.wireOp",EDGE,"E1.top");Q25=makeQuery(id+"F1.opExtrude","CAP_EDGE",EDGE,{"disambiguationData":[OSD([subQ0]),TDD([makeQuery(id+"F0.imprint","IMPRINT",EDGE,{"disambiguationData":[TD([[makeQuery(id+"F0.imprint","INTERSECT",VERTEX,{"derivedFrom":[subQ0,sQuery(id+"F0.wireOp",EDGE,"E1.right")]}),1.0]])],"derivedFrom":subQ0})])],"isStart":false});}
            var Q26;
            {var subQ0=sQuery(id+"F0.wireOp",EDGE,"E0.right");Q26=makeQuery(id+"F1.opExtrude","CAP_EDGE",EDGE,{"disambiguationData":[OSD([subQ0]),TDD([makeQuery(id+"F0.imprint","IMPRINT",EDGE,{"disambiguationData":[TD([[makeQuery(id+"F0.imprint","INTERSECT",VERTEX,{"derivedFrom":[subQ0,sQuery(id+"F0.wireOp",EDGE,"E1.top")]}),-1.0]])],"derivedFrom":subQ0})])],"isStart":false});}
            var Q27;
            {var subQ0=sQuery(id+"F0.wireOp",EDGE,"E2.0.1.0");Q27=makeQuery(id+"F1.opExtrude","CAP_EDGE",EDGE,{"disambiguationData":[OSD([subQ0]),TDD([makeQuery(id+"F0.imprint","IMPRINT",EDGE,{"disambiguationData":[TD([[makeQuery(id+"F0.imprint","INTERSECT",VERTEX,{"derivedFrom":[subQ0,sQuery(id+"F0.wireOp",EDGE,"E2.0.1.2")]}),1.0]])],"derivedFrom":subQ0})])],"isStart":false});}
            var Q28;
            {var subQ0=sQuery(id+"F0.wireOp",EDGE,"E2.0.1.1");Q28=makeQuery(id+"F1.opExtrude","CAP_EDGE",EDGE,{"disambiguationData":[OSD([subQ0]),TDD([makeQuery(id+"F0.imprint","IMPRINT",EDGE,{"disambiguationData":[TD([[makeQuery(id+"F0.imprint","INTERSECT",VERTEX,{"derivedFrom":[subQ0,sQuery(id+"F0.wireOp",EDGE,"E2.0.1.2")]}),1.0]])],"derivedFrom":subQ0})])],"isStart":false});}
            var Q29;
            {var subQ0=sQuery(id+"F0.wireOp",EDGE,"E0.right");Q29=makeQuery(id+"F1.opExtrude","CAP_EDGE",EDGE,{"disambiguationData":[OSD([subQ0]),TDD([makeQuery(id+"F0.imprint","IMPRINT",EDGE,{"disambiguationData":[TD([[makeQuery(id+"F0.imprint","INTERSECT",VERTEX,{"derivedFrom":[subQ0,sQuery(id+"F0.wireOp",EDGE,"E2.0.1.1")]}),-1.0]])],"derivedFrom":subQ0})])],"isStart":false});}
            var Q30;
            {var subQ0=sQuery(id+"F0.wireOp",EDGE,"E2.1.0.0");Q30=makeQuery(id+"F1.opExtrude","CAP_EDGE",EDGE,{"disambiguationData":[OSD([subQ0]),TDD([makeQuery(id+"F0.imprint","IMPRINT",EDGE,{"disambiguationData":[TD([[makeQuery(id+"F0.imprint","INTERSECT",VERTEX,{"derivedFrom":[subQ0,sQuery(id+"F0.wireOp",EDGE,"E2.1.0.2")]}),1.0]])],"derivedFrom":subQ0})])],"isStart":false});}
            var Q31;
            {var subQ0=sQuery(id+"F0.wireOp",EDGE,"E2.1.0.1");Q31=makeQuery(id+"F1.opExtrude","CAP_EDGE",EDGE,{"disambiguationData":[OSD([subQ0]),TDD([makeQuery(id+"F0.imprint","IMPRINT",EDGE,{"disambiguationData":[TD([[makeQuery(id+"F0.imprint","INTERSECT",VERTEX,{"derivedFrom":[subQ0,sQuery(id+"F0.wireOp",EDGE,"E2.1.0.2")]}),1.0]])],"derivedFrom":subQ0})])],"isStart":false});}
            var Q32;
            {var subQ0=sQuery(id+"F0.wireOp",EDGE,"E0.right");Q32=makeQuery(id+"F1.opExtrude","CAP_EDGE",EDGE,{"disambiguationData":[OSD([subQ0]),TDD([makeQuery(id+"F0.imprint","IMPRINT",EDGE,{"disambiguationData":[TD([[makeQuery(id+"F0.imprint","INTERSECT",VERTEX,{"derivedFrom":[subQ0,sQuery(id+"F0.wireOp",EDGE,"E2.1.0.1")]}),-1.0]])],"derivedFrom":subQ0})])],"isStart":false});}
            var Q33;
            {var subQ0=sQuery(id+"F0.wireOp",EDGE,"E2.1.1.0");Q33=makeQuery(id+"F1.opExtrude","CAP_EDGE",EDGE,{"disambiguationData":[OSD([subQ0]),TDD([makeQuery(id+"F0.imprint","IMPRINT",EDGE,{"disambiguationData":[TD([[makeQuery(id+"F0.imprint","INTERSECT",VERTEX,{"derivedFrom":[subQ0,sQuery(id+"F0.wireOp",EDGE,"E2.1.1.2")]}),1.0]])],"derivedFrom":subQ0})])],"isStart":false});}
            var Q34;
            {var subQ0=sQuery(id+"F0.wireOp",EDGE,"E2.1.1.1");Q34=makeQuery(id+"F1.opExtrude","CAP_EDGE",EDGE,{"disambiguationData":[OSD([subQ0]),TDD([makeQuery(id+"F0.imprint","IMPRINT",EDGE,{"disambiguationData":[TD([[makeQuery(id+"F0.imprint","INTERSECT",VERTEX,{"derivedFrom":[subQ0,sQuery(id+"F0.wireOp",EDGE,"E2.1.1.2")]}),1.0]])],"derivedFrom":subQ0})])],"isStart":false});}
            var Q35;
            {var subQ0=sQuery(id+"F0.wireOp",EDGE,"E0.right");Q35=makeQuery(id+"F1.opExtrude","CAP_EDGE",EDGE,{"disambiguationData":[OSD([subQ0]),TDD([makeQuery(id+"F0.imprint","IMPRINT",EDGE,{"disambiguationData":[TD([[makeQuery(id+"F0.imprint","INTERSECT",VERTEX,{"derivedFrom":[subQ0,sQuery(id+"F0.wireOp",EDGE,"E2.1.1.1")]}),-1.0]])],"derivedFrom":subQ0})])],"isStart":false});}
            var Q36;
            {var subQ0=sQuery(id+"F0.wireOp",EDGE,"E2.2.0.0");Q36=makeQuery(id+"F1.opExtrude","CAP_EDGE",EDGE,{"disambiguationData":[OSD([subQ0]),TDD([makeQuery(id+"F0.imprint","IMPRINT",EDGE,{"disambiguationData":[TD([[makeQuery(id+"F0.imprint","INTERSECT",VERTEX,{"derivedFrom":[subQ0,sQuery(id+"F0.wireOp",EDGE,"E2.2.0.2")]}),1.0]])],"derivedFrom":subQ0})])],"isStart":false});}
            var Q37;
            {var subQ0=sQuery(id+"F0.wireOp",EDGE,"E2.0.1.0");Q37=makeQuery(id+"F1.opExtrude","CAP_EDGE",EDGE,{"disambiguationData":[OSD([subQ0]),TDD([makeQuery(id+"F0.imprint","IMPRINT",EDGE,{"disambiguationData":[TD([[makeQuery(id+"F0.imprint","INTERSECT",VERTEX,{"derivedFrom":[subQ0,sQuery(id+"F0.wireOp",EDGE,"E2.0.1.3")]}),-1.0]])],"derivedFrom":subQ0})])],"isStart":false});}
            var Q38;
            {var subQ0=sQuery(id+"F0.wireOp",EDGE,"E2.0.1.1");Q38=makeQuery(id+"F1.opExtrude","CAP_EDGE",EDGE,{"disambiguationData":[OSD([subQ0]),TDD([makeQuery(id+"F0.imprint","IMPRINT",EDGE,{"disambiguationData":[TD([[makeQuery(id+"F0.imprint","INTERSECT",VERTEX,{"derivedFrom":[subQ0,sQuery(id+"F0.wireOp",EDGE,"E2.0.1.3")]}),-1.0]])],"derivedFrom":subQ0})])],"isStart":false});}
            var Q39;
            {var subQ0=sQuery(id+"F0.wireOp",EDGE,"E0.left");Q39=makeQuery(id+"F1.opExtrude","CAP_EDGE",EDGE,{"disambiguationData":[OSD([subQ0]),TDD([makeQuery(id+"F0.imprint","IMPRINT",EDGE,{"disambiguationData":[TD([[makeQuery(id+"F0.imprint","INTERSECT",VERTEX,{"derivedFrom":[subQ0,sQuery(id+"F0.wireOp",EDGE,"E2.0.1.1")]}),-1.0]])],"derivedFrom":subQ0})])],"isStart":false});}
            var Q40;
            {var subQ0=sQuery(id+"F0.wireOp",EDGE,"E2.1.0.0");Q40=makeQuery(id+"F1.opExtrude","CAP_EDGE",EDGE,{"disambiguationData":[OSD([subQ0]),TDD([makeQuery(id+"F0.imprint","IMPRINT",EDGE,{"disambiguationData":[TD([[makeQuery(id+"F0.imprint","INTERSECT",VERTEX,{"derivedFrom":[subQ0,sQuery(id+"F0.wireOp",EDGE,"E2.1.0.3")]}),-1.0]])],"derivedFrom":subQ0})])],"isStart":false});}
            var Q41;
            {var subQ0=sQuery(id+"F0.wireOp",EDGE,"E2.1.0.1");Q41=makeQuery(id+"F1.opExtrude","CAP_EDGE",EDGE,{"disambiguationData":[OSD([subQ0]),TDD([makeQuery(id+"F0.imprint","IMPRINT",EDGE,{"disambiguationData":[TD([[makeQuery(id+"F0.imprint","INTERSECT",VERTEX,{"derivedFrom":[subQ0,sQuery(id+"F0.wireOp",EDGE,"E2.1.0.3")]}),-1.0]])],"derivedFrom":subQ0})])],"isStart":false});}
            var Q42;
            {var subQ0=sQuery(id+"F0.wireOp",EDGE,"E0.left");Q42=makeQuery(id+"F1.opExtrude","CAP_EDGE",EDGE,{"disambiguationData":[OSD([subQ0]),TDD([makeQuery(id+"F0.imprint","IMPRINT",EDGE,{"disambiguationData":[TD([[makeQuery(id+"F0.imprint","INTERSECT",VERTEX,{"derivedFrom":[subQ0,sQuery(id+"F0.wireOp",EDGE,"E2.1.0.1")]}),-1.0]])],"derivedFrom":subQ0})])],"isStart":false});}
            var Q43;
            {var subQ0=sQuery(id+"F0.wireOp",EDGE,"E2.1.1.0");Q43=makeQuery(id+"F1.opExtrude","CAP_EDGE",EDGE,{"disambiguationData":[OSD([subQ0]),TDD([makeQuery(id+"F0.imprint","IMPRINT",EDGE,{"disambiguationData":[TD([[makeQuery(id+"F0.imprint","INTERSECT",VERTEX,{"derivedFrom":[subQ0,sQuery(id+"F0.wireOp",EDGE,"E2.1.1.3")]}),-1.0]])],"derivedFrom":subQ0})])],"isStart":false});}
            var Q44;
            {var subQ0=sQuery(id+"F0.wireOp",EDGE,"E2.1.1.1");Q44=makeQuery(id+"F1.opExtrude","CAP_EDGE",EDGE,{"disambiguationData":[OSD([subQ0]),TDD([makeQuery(id+"F0.imprint","IMPRINT",EDGE,{"disambiguationData":[TD([[makeQuery(id+"F0.imprint","INTERSECT",VERTEX,{"derivedFrom":[subQ0,sQuery(id+"F0.wireOp",EDGE,"E2.1.1.3")]}),-1.0]])],"derivedFrom":subQ0})])],"isStart":false});}
            var Q45;
            {var subQ0=sQuery(id+"F0.wireOp",EDGE,"E0.left");Q45=makeQuery(id+"F1.opExtrude","CAP_EDGE",EDGE,{"disambiguationData":[OSD([subQ0]),TDD([makeQuery(id+"F0.imprint","IMPRINT",EDGE,{"disambiguationData":[TD([[makeQuery(id+"F0.imprint","INTERSECT",VERTEX,{"derivedFrom":[subQ0,sQuery(id+"F0.wireOp",EDGE,"E2.1.1.1")]}),-1.0]])],"derivedFrom":subQ0})])],"isStart":false});}
            var Q46;
            {var subQ0=sQuery(id+"F0.wireOp",EDGE,"E2.2.0.0");Q46=makeQuery(id+"F1.opExtrude","CAP_EDGE",EDGE,{"disambiguationData":[OSD([subQ0]),TDD([makeQuery(id+"F0.imprint","IMPRINT",EDGE,{"disambiguationData":[TD([[makeQuery(id+"F0.imprint","INTERSECT",VERTEX,{"derivedFrom":[subQ0,sQuery(id+"F0.wireOp",EDGE,"E2.2.0.3")]}),-1.0]])],"derivedFrom":subQ0})])],"isStart":false});}
            chamfer(context, id + "F3", {"entities" : qUnion([Q0, Q1, Q2, Q3, Q4, Q5, Q6, Q7, Q8, Q9, Q10, Q11, Q12, Q13, Q14, Q15, Q16, Q17, Q18, Q19, Q20, Q21, Q22, Q23, Q24, Q25, Q26, Q27, Q28, Q29, Q30, Q31, Q32, Q33, Q34, Q35, Q36, Q37, Q38, Q39, Q40, Q41, Q42, Q43, Q44, Q45, Q46]), "width" : 2.54 * mm, "tangentPropagation" : true});
        }
        {
            var Q0;
            Q0=makeQuery(id+"F1.opExtrude","SWEPT_EDGE",EDGE,{"disambiguationData":[OSD([sQuery(id+"F0.wireOp",EDGE,"E8.bottom"),sQuery(id+"F0.wireOp",EDGE,"E8.left")])]});
            var Q1;
            Q1=makeQuery(id+"F1.opExtrude","CAP_EDGE",EDGE,{"disambiguationData":[OSD([sQuery(id+"F0.wireOp",EDGE,"E8.bottom")])],"isStart":false});
            var Q2;
            Q2=makeQuery(id+"F1.opExtrude","SWEPT_EDGE",EDGE,{"disambiguationData":[OSD([sQuery(id+"F0.wireOp",EDGE,"E8.bottom"),sQuery(id+"F0.wireOp",EDGE,"E8.right")])]});
            var Q3;
            Q3=makeQuery(id+"F1.opExtrude","CAP_EDGE",EDGE,{"disambiguationData":[OSD([sQuery(id+"F0.wireOp",EDGE,"E8.bottom")])],"isStart":true});
            var Q4;
            Q4=makeQuery(id+"F1.opExtrude","CAP_EDGE",EDGE,{"disambiguationData":[OSD([sQuery(id+"F0.wireOp",EDGE,"E8.left")])],"isStart":false});
            var Q5;
            Q5=makeQuery(id+"F1.opExtrude","CAP_EDGE",EDGE,{"disambiguationData":[OSD([sQuery(id+"F0.wireOp",EDGE,"E8.left")])],"isStart":true});
            var Q6;
            Q6=makeQuery(id+"F1.opExtrude","CAP_EDGE",EDGE,{"disambiguationData":[OSD([sQuery(id+"F0.wireOp",EDGE,"E8.right")])],"isStart":false});
            var Q7;
            Q7=makeQuery(id+"F1.opExtrude","CAP_EDGE",EDGE,{"disambiguationData":[OSD([sQuery(id+"F0.wireOp",EDGE,"E8.right")])],"isStart":true});
            var Q8;
            Q8=makeQuery(id+"F1.opExtrude","CAP_EDGE",EDGE,{"disambiguationData":[OSD([sQuery(id+"F0.wireOp",EDGE,"E9.left")])],"isStart":true});
            var Q9;
            Q9=makeQuery(id+"F1.opExtrude","CAP_EDGE",EDGE,{"disambiguationData":[OSD([sQuery(id+"F0.wireOp",EDGE,"E9.right")])],"isStart":true});
            var Q10;
            Q10=makeQuery(id+"F1.opExtrude","CAP_EDGE",EDGE,{"disambiguationData":[OSD([sQuery(id+"F0.wireOp",EDGE,"E9.right")])],"isStart":false});
            var Q11;
            Q11=makeQuery(id+"F1.opExtrude","SWEPT_EDGE",EDGE,{"disambiguationData":[OSD([sQuery(id+"F0.wireOp",EDGE,"E9.bottom"),sQuery(id+"F0.wireOp",EDGE,"E9.right")])]});
            var Q12;
            Q12=makeQuery(id+"F1.opExtrude","CAP_EDGE",EDGE,{"disambiguationData":[OSD([sQuery(id+"F0.wireOp",EDGE,"E9.bottom")])],"isStart":false});
            var Q13;
            Q13=makeQuery(id+"F1.opExtrude","SWEPT_EDGE",EDGE,{"disambiguationData":[OSD([sQuery(id+"F0.wireOp",EDGE,"E9.bottom"),sQuery(id+"F0.wireOp",EDGE,"E9.left")])]});
            var Q14;
            Q14=makeQuery(id+"F1.opExtrude","CAP_EDGE",EDGE,{"disambiguationData":[OSD([sQuery(id+"F0.wireOp",EDGE,"E9.bottom")])],"isStart":true});
            var Q15;
            Q15=makeQuery(id+"F1.opExtrude","CAP_EDGE",EDGE,{"disambiguationData":[OSD([sQuery(id+"F0.wireOp",EDGE,"E9.left")])],"isStart":false});
            var Q16;
            Q16=makeQuery(id+"F1.opExtrude","CAP_EDGE",EDGE,{"disambiguationData":[OSD([sQuery(id+"F0.wireOp",EDGE,"E4.MirrorCS")])],"isStart":false});
            var Q17;
            Q17=makeQuery(id+"F1.opExtrude","CAP_EDGE",EDGE,{"disambiguationData":[OSD([sQuery(id+"F0.wireOp",EDGE,"E4.MirrorCS")])],"isStart":true});
            var Q18;
            Q18=makeQuery(id+"F1.opExtrude","CAP_EDGE",EDGE,{"disambiguationData":[OSD([sQuery(id+"F0.wireOp",EDGE,"E3.right")])],"isStart":true});
            var Q19;
            Q19=makeQuery(id+"F1.opExtrude","CAP_EDGE",EDGE,{"disambiguationData":[OSD([sQuery(id+"F0.wireOp",EDGE,"E3.right")])],"isStart":false});
            chamfer(context, id + "F4", {"entities" : qUnion([Q0, Q1, Q2, Q3, Q4, Q5, Q6, Q7, Q8, Q9, Q10, Q11, Q12, Q13, Q14, Q15, Q16, Q17, Q18, Q19]), "width" : 3.3 * mm, "tangentPropagation" : true});
        }
        {
            var Q0;
            {var subQ0=sQuery(id+"F0.wireOp",EDGE,"E2.1.1.0");Q0=makeQuery(id+"F1.opExtrude","CAP_EDGE",EDGE,{"disambiguationData":[OSD([subQ0]),TDD([makeQuery(id+"F0.imprint","IMPRINT",EDGE,{"disambiguationData":[TD([[makeQuery(id+"F0.imprint","INTERSECT",VERTEX,{"derivedFrom":[subQ0,sQuery(id+"F0.wireOp",EDGE,"E2.1.1.3")]}),-1.0]])],"derivedFrom":subQ0})])],"isStart":true});}
            chamfer(context, id + "F5", {"entities" : qUnion([Q0]), "width" : 2.54 * mm, "tangentPropagation" : true});
        }
    });
